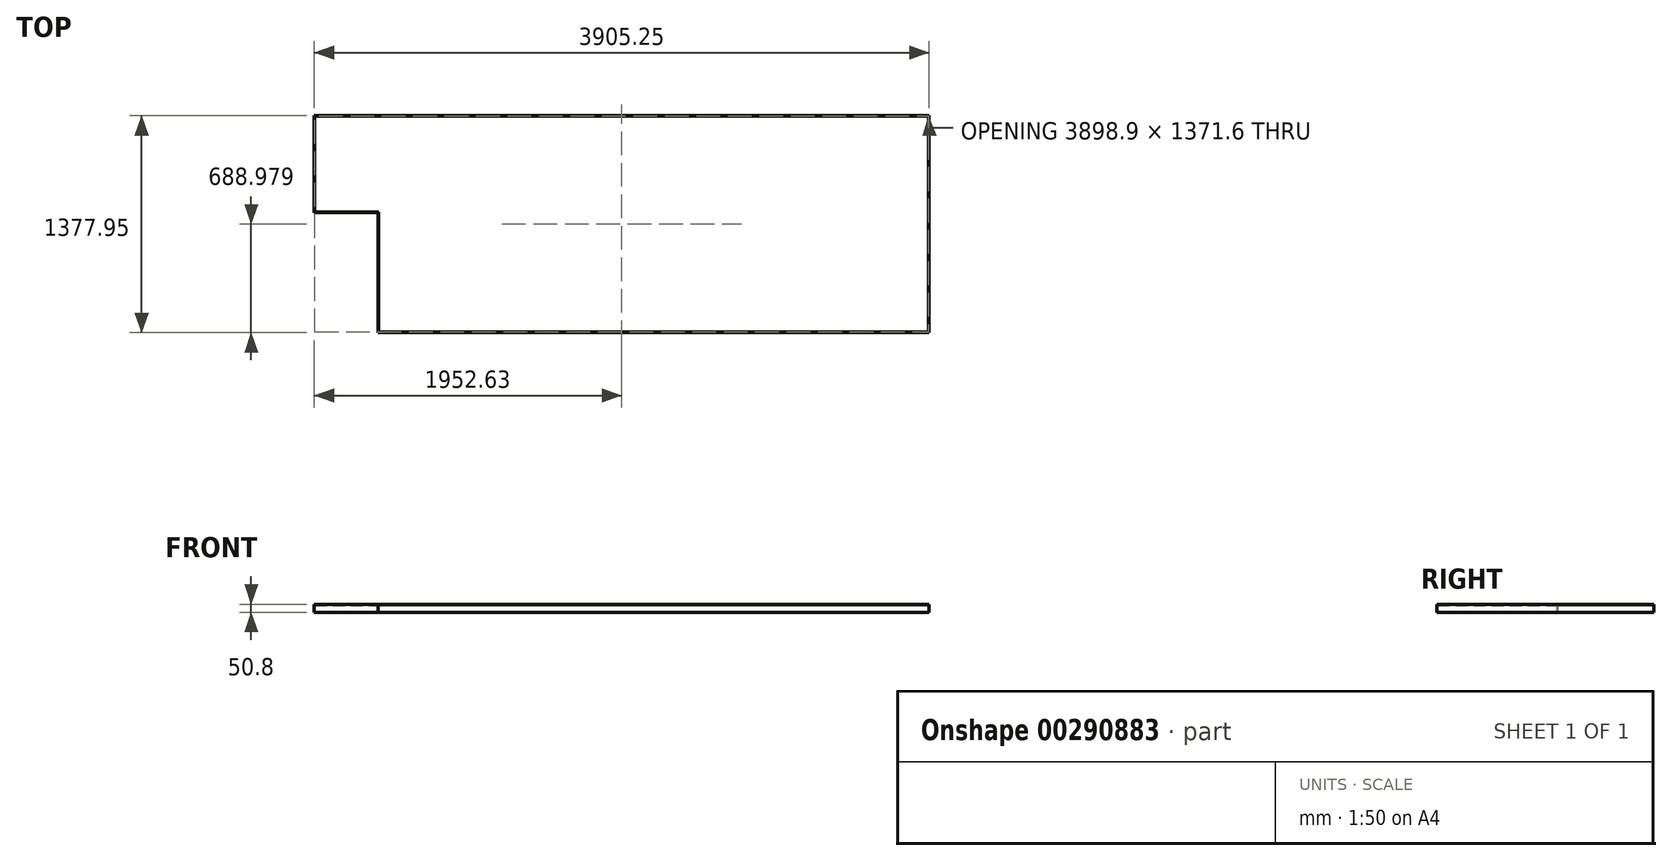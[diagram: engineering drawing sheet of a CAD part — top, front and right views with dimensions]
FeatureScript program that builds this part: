
annotation { "Feature Type Name" : "Feature", "Feature Type Description" : "" }
export const myFeature = defineFeature(function(context is Context, id is Id, definition is map)
    precondition{}
    {
        {
            var Q0;
            Q0=qCreatedBy(makeId("Top.planeOp"),FACE);
            var sketch = newSketch(context, id + "F0", { "sketchPlane" : qUnion([Q0])});
            skLineSegment(sketch, "E0.bottom", {"start": v(1070.18, -132.63) * mm, "end": v(4562.68, -132.63) * mm});
            skLineSegment(sketch, "E0.top", {"start": v(663.78, 1238.97) * mm, "end": v(4562.68, 1238.97) * mm});
            skLineSegment(sketch, "E0.left", {"start": v(663.78, 629.37) * mm, "end": v(663.78, 1238.97) * mm});
            skLineSegment(sketch, "E0.right", {"start": v(4562.68, -132.63) * mm, "end": v(4562.68, 1238.97) * mm});
            skLineSegment(sketch, "E1.bottom", {"start": v(663.78, 629.37) * mm, "end": v(1070.18, 629.37) * mm});
            skLineSegment(sketch, "E1.right", {"start": v(1070.18, 629.37) * mm, "end": v(1070.18, -132.63) * mm});
            skLineSegment(sketch, "E2.0", {"start": v(660.6, 626.2) * mm, "end": v(660.6, 1242.14) * mm});
            skLineSegment(sketch, "E2.1", {"start": v(4565.85, -135.8) * mm, "end": v(4565.85, 1242.14) * mm});
            skLineSegment(sketch, "E2.2", {"start": v(1067, -135.8) * mm, "end": v(4565.85, -135.8) * mm});
            skLineSegment(sketch, "E2.3", {"start": v(660.6, 1242.14) * mm, "end": v(4565.85, 1242.14) * mm});
            skLineSegment(sketch, "E2.4", {"start": v(1067, 626.2) * mm, "end": v(1067, -135.8) * mm});
            skLineSegment(sketch, "E2.5", {"start": v(660.6, 626.2) * mm, "end": v(1067, 626.2) * mm});
            skSolve(sketch);
        }
        {
            var Q0;
            Q0 = qSketchRegion(id + "F0", true);
            extrude(context, id + "F1", {"entities" : qUnion([Q0]), "depth" : 50.8 * mm});
        }
        {
            var Q0;
            Q0=makeQuery(id+"F1.opExtrude","CAP_FACE",FACE,{"disambiguationData":[OSD([sQuery(id+"F0.wireOp",EDGE,"E0.bottom"),sQuery(id+"F0.wireOp",EDGE,"E0.top"),sQuery(id+"F0.wireOp",EDGE,"E0.left"),sQuery(id+"F0.wireOp",EDGE,"E0.right"),sQuery(id+"F0.wireOp",EDGE,"E1.bottom"),sQuery(id+"F0.wireOp",EDGE,"E1.right"),sQuery(id+"F0.wireOp",EDGE,"E2.0"),sQuery(id+"F0.wireOp",EDGE,"E2.1"),sQuery(id+"F0.wireOp",EDGE,"E2.2"),sQuery(id+"F0.wireOp",EDGE,"E2.3"),sQuery(id+"F0.wireOp",EDGE,"E2.4"),sQuery(id+"F0.wireOp",EDGE,"E2.5")])],"isStart":true});
            var sketch = newSketch(context, id + "F2", { "sketchPlane" : qUnion([Q0])});
            skLineSegment(sketch, "E3", {"start": v(663.78, -629.37) * mm, "end": v(1070.18, -629.37) * mm});
            skLineSegment(sketch, "E4", {"start": v(1070.18, -629.37) * mm, "end": v(1070.18, 132.63) * mm});
            skLineSegment(sketch, "E5", {"start": v(1070.18, 132.63) * mm, "end": v(4562.68, 132.63) * mm});
            skLineSegment(sketch, "E6", {"start": v(4562.68, 132.63) * mm, "end": v(4562.68, -1238.97) * mm});
            skLineSegment(sketch, "E7", {"start": v(4562.68, -1238.97) * mm, "end": v(663.78, -1238.97) * mm});
            skLineSegment(sketch, "E8", {"start": v(663.78, -1238.97) * mm, "end": v(663.78, -629.37) * mm});
            skSolve(sketch);
        }
        {
            var Q0;
            Q0 = qSketchRegion(id + "F2", true);
            extrude(context, id + "F3", {"entities" : qUnion([Q0]), "oppositeDirection" : true, "depth" : 44.45 * mm});
        }
        {
            var Q0;
            Q0=makeQuery(id+"F3.opExtrude","CAP_FACE",FACE,{"disambiguationData":[OSD([sQuery(id+"F2.wireOp",EDGE,"E3"),sQuery(id+"F2.wireOp",EDGE,"E4"),sQuery(id+"F2.wireOp",EDGE,"E5"),sQuery(id+"F2.wireOp",EDGE,"E6"),sQuery(id+"F2.wireOp",EDGE,"E7"),sQuery(id+"F2.wireOp",EDGE,"E8")])],"isStart":false});
            var sketch = newSketch(context, id + "F4", { "sketchPlane" : qUnion([Q0])});
            skLineSegment(sketch, "E9", {"start": v(663.78, 1238.97) * mm, "end": v(663.78, 629.37) * mm});
            skLineSegment(sketch, "E10", {"start": v(663.78, 629.37) * mm, "end": v(1070.18, 629.37) * mm});
            skLineSegment(sketch, "E11", {"start": v(1070.18, 629.37) * mm, "end": v(1070.18, -132.63) * mm});
            skLineSegment(sketch, "E12", {"start": v(1070.18, -132.63) * mm, "end": v(4562.68, -132.63) * mm});
            skLineSegment(sketch, "E13", {"start": v(4562.68, -132.63) * mm, "end": v(4562.68, 1238.97) * mm});
            skLineSegment(sketch, "E14", {"start": v(4562.68, 1238.97) * mm, "end": v(663.78, 1238.97) * mm});
            skSolve(sketch);
        }
        {
            var Q0;
            Q0 = qSketchRegion(id + "F4", true);
            extrude(context, id + "F5", {"entities" : qUnion([Q0]), "depth" : 6.35 * mm});
        }
    });
